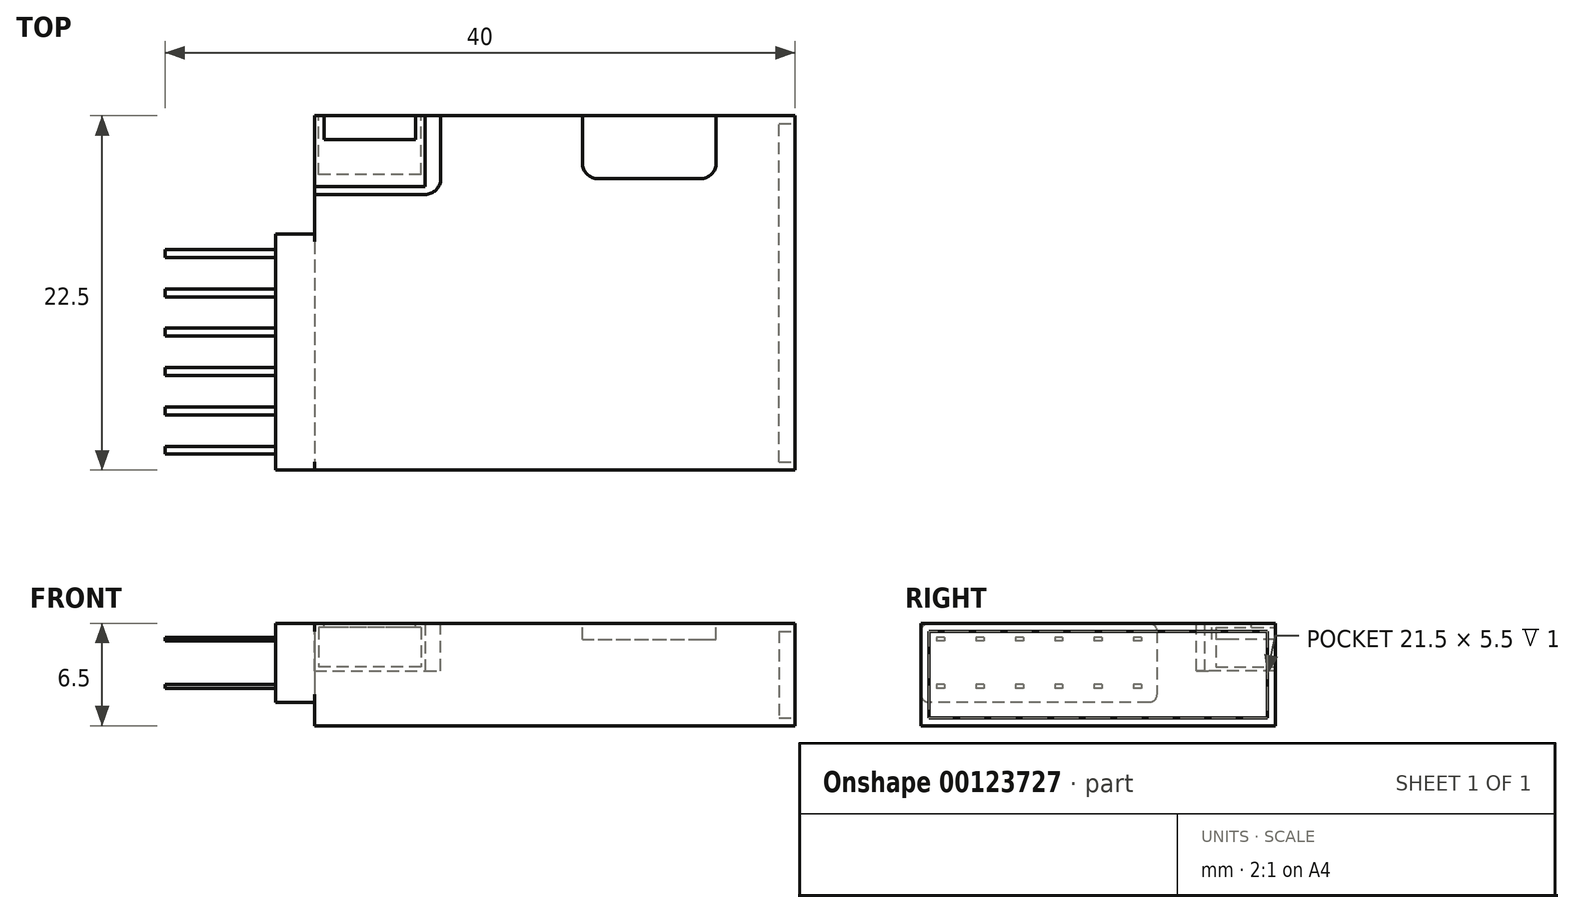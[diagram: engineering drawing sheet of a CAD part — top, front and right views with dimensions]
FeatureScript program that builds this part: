
annotation { "Feature Type Name" : "Feature", "Feature Type Description" : "" }
export const myFeature = defineFeature(function(context is Context, id is Id, definition is map)
    precondition{}
    {
        {
            var Q0;
            Q0=qCreatedBy(makeId("Top.planeOp"),FACE);
            var sketch = newSketch(context, id + "F0", { "sketchPlane" : qUnion([Q0])});
            skLineSegment(sketch, "E0.bottom", {"start": v(-15.25, 11.25) * mm, "end": v(15.25, 11.25) * mm});
            skLineSegment(sketch, "E0.top", {"start": v(-15.25, -11.25) * mm, "end": v(15.25, -11.25) * mm});
            skLineSegment(sketch, "E0.left", {"start": v(-15.25, 11.25) * mm, "end": v(-15.25, -11.25) * mm});
            skLineSegment(sketch, "E0.right", {"start": v(15.25, 11.25) * mm, "end": v(15.25, -11.25) * mm});
            skSolve(sketch);
        }
        {
            var Q0;
            Q0=qSketchRegion(id+"F0",true);
            extrude(context, id + "F1", {"entities" : qUnion([Q0]), "depth" : 6.5 * mm});
        }
        {
            var Q0;
            Q0=makeQuery(id+"F1.opExtrude","CAP_FACE",FACE,{"disambiguationData":[OSD([sQuery(id+"F0.wireOp",EDGE,"E0.bottom"),sQuery(id+"F0.wireOp",EDGE,"E0.top"),sQuery(id+"F0.wireOp",EDGE,"E0.left"),sQuery(id+"F0.wireOp",EDGE,"E0.right")])],"isStart":false});
            var sketch = newSketch(context, id + "F2", { "sketchPlane" : qUnion([Q0])});
            skLineSegment(sketch, "E1.bottom", {"start": v(-15.25, 11.25) * mm, "end": v(-7.25, 11.25) * mm});
            skLineSegment(sketch, "E1.top", {"start": v(-15.25, 6.25) * mm, "end": v(-8.25, 6.25) * mm});
            skLineSegment(sketch, "E1.left", {"start": v(-15.25, 11.25) * mm, "end": v(-15.25, 6.25) * mm});
            skLineSegment(sketch, "E1.right", {"start": v(-7.25, 11.25) * mm, "end": v(-7.25, 7.25) * mm});
            skPoint(sketch, "E2.visualSharp", {"position": v(-7.25, 6.25) * mm});
            skArc(sketch, "E2.filletArc", {"start": v(-8.25, 6.25) * mm, "mid": v(-7.54, 6.54) * mm, "end": v(-7.25, 7.25) * mm});
            skSolve(sketch);
        }
        {
            var Q0;
            Q0=qSketchRegion(id+"F2",true);
            extrude(context, id + "F3", {"entities" : qUnion([Q0]), "operationType" : NewBodyOperationType.REMOVE, "oppositeDirection" : true, "depth" : 3 * mm});
        }
        {
            var Q0;
            Q0=makeQuery(id+"F3.boolean.opBoolean","COPY",FACE,{"derivedFrom":makeQuery(id+"F3.opExtrude","CAP_FACE",FACE,{"disambiguationData":[OSD([sQuery(id+"F2.wireOp",EDGE,"E1.bottom"),sQuery(id+"F2.wireOp",EDGE,"E1.top"),sQuery(id+"F2.wireOp",EDGE,"E1.left"),sQuery(id+"F2.wireOp",EDGE,"E1.right"),sQuery(id+"F2.wireOp",EDGE,"E2.filletArc")])],"isStart":false})});
            var sketch = newSketch(context, id + "F4", { "sketchPlane" : qUnion([Q0])});
            skLineSegment(sketch, "E3.bottom", {"start": v(-15.25, 11.25) * mm, "end": v(-8.25, 11.25) * mm});
            skLineSegment(sketch, "E3.top", {"start": v(-15.25, 6.75) * mm, "end": v(-8.25, 6.75) * mm});
            skLineSegment(sketch, "E3.left", {"start": v(-15.25, 11.25) * mm, "end": v(-15.25, 6.75) * mm});
            skLineSegment(sketch, "E3.right", {"start": v(-8.25, 11.25) * mm, "end": v(-8.25, 6.75) * mm});
            skSolve(sketch);
        }
        {
            var Q0;
            Q0=qSketchRegion(id+"F4",true);
            extrude(context, id + "F5", {"entities" : qUnion([Q0]), "operationType" : NewBodyOperationType.ADD, "depth" : 3 * mm});
        }
        {
            var Q0;
            Q0=makeQuery(id+"F5.boolean.opBoolean","MERGE",FACE,{"derivedFrom":[makeQuery(id+"F1.opExtrude","SWEPT_FACE",FACE,{"disambiguationData":[OSD([sQuery(id+"F0.wireOp",EDGE,"E0.bottom")])]}),makeQuery(id+"F5.opExtrude","SWEPT_FACE",FACE,{"disambiguationData":[OSD([sQuery(id+"F4.wireOp",EDGE,"E3.bottom")])]})]});
            var sketch = newSketch(context, id + "F6", { "sketchPlane" : qUnion([Q0])});
            skLineSegment(sketch, "E4.bottom", {"start": v(8.5, 6.25) * mm, "end": v(15, 6.25) * mm});
            skLineSegment(sketch, "E4.top", {"start": v(8.5, 3.75) * mm, "end": v(15, 3.75) * mm});
            skLineSegment(sketch, "E4.left", {"start": v(8.5, 6.25) * mm, "end": v(8.5, 3.75) * mm});
            skLineSegment(sketch, "E4.right", {"start": v(15, 6.25) * mm, "end": v(15, 3.75) * mm});
            skSolve(sketch);
        }
        {
            var Q0;
            Q0=qSketchRegion(id+"F6",true);
            extrude(context, id + "F7", {"entities" : qUnion([Q0]), "operationType" : NewBodyOperationType.REMOVE, "oppositeDirection" : true, "depth" : 3.75 * mm});
        }
        {
            var Q0;
            Q0=makeQuery(id+"F5.opExtrude","CAP_FACE",FACE,{"disambiguationData":[OSD([sQuery(id+"F4.wireOp",EDGE,"E3.bottom"),sQuery(id+"F4.wireOp",EDGE,"E3.top"),sQuery(id+"F4.wireOp",EDGE,"E3.left"),sQuery(id+"F4.wireOp",EDGE,"E3.right")])],"isStart":false});
            var sketch = newSketch(context, id + "F8", { "sketchPlane" : qUnion([Q0])});
            skLineSegment(sketch, "E5.bottom", {"start": v(-14.65, 11.25) * mm, "end": v(-8.85, 11.25) * mm});
            skLineSegment(sketch, "E5.top", {"start": v(-14.65, 9.75) * mm, "end": v(-8.85, 9.75) * mm});
            skLineSegment(sketch, "E5.left", {"start": v(-14.65, 11.25) * mm, "end": v(-14.65, 9.75) * mm});
            skLineSegment(sketch, "E5.right", {"start": v(-8.85, 11.25) * mm, "end": v(-8.85, 9.75) * mm});
            skSolve(sketch);
        }
        {
            var Q0;
            Q0=qSketchRegion(id+"F8",true);
            extrude(context, id + "F9", {"entities" : qUnion([Q0]), "operationType" : NewBodyOperationType.REMOVE, "oppositeDirection" : true, "depth" : 0.5 * mm});
        }
        {
            var Q0;
            Q0=makeQuery(id+"F1.opExtrude","CAP_FACE",FACE,{"disambiguationData":[OSD([sQuery(id+"F0.wireOp",EDGE,"E0.bottom"),sQuery(id+"F0.wireOp",EDGE,"E0.top"),sQuery(id+"F0.wireOp",EDGE,"E0.left"),sQuery(id+"F0.wireOp",EDGE,"E0.right")])],"isStart":false});
            var sketch = newSketch(context, id + "F10", { "sketchPlane" : qUnion([Q0])});
            skLineSegment(sketch, "E6.bottom", {"start": v(1.75, 11.25) * mm, "end": v(10.25, 11.25) * mm});
            skLineSegment(sketch, "E6.top", {"start": v(2.75, 7.25) * mm, "end": v(9.25, 7.25) * mm});
            skLineSegment(sketch, "E6.left", {"start": v(1.75, 11.25) * mm, "end": v(1.75, 8.25) * mm});
            skLineSegment(sketch, "E6.right", {"start": v(10.25, 11.25) * mm, "end": v(10.25, 8.25) * mm});
            skPoint(sketch, "E7.visualSharp", {"position": v(1.75, 7.25) * mm});
            skArc(sketch, "E7.filletArc", {"start": v(1.75, 8.25) * mm, "mid": v(2.04, 7.54) * mm, "end": v(2.75, 7.25) * mm});
            skPoint(sketch, "E8.visualSharp", {"position": v(10.25, 7.25) * mm});
            skArc(sketch, "E8.filletArc", {"start": v(9.25, 7.25) * mm, "mid": v(9.96, 7.54) * mm, "end": v(10.25, 8.25) * mm});
            skSolve(sketch);
        }
        {
            var Q0;
            Q0=makeQuery(id+"F10.imprint","IMPRINT",FACE,{"disambiguationData":[TD([[makeQuery(id+"F10.imprint","IMPRINT",EDGE,{"derivedFrom":sQuery(id+"F10.wireOp",EDGE,"E6.bottom")}),-1.0]])]});
            extrude(context, id + "F11", {"entities" : qUnion([Q0]), "operationType" : NewBodyOperationType.REMOVE, "oppositeDirection" : true, "depth" : 1 * mm});
        }
        {
            var Q0;
            Q0=makeQuery(id+"F5.boolean.opBoolean","MERGE",FACE,{"derivedFrom":[makeQuery(id+"F1.opExtrude","SWEPT_FACE",FACE,{"disambiguationData":[OSD([sQuery(id+"F0.wireOp",EDGE,"E0.left")])]}),makeQuery(id+"F5.opExtrude","SWEPT_FACE",FACE,{"disambiguationData":[OSD([sQuery(id+"F4.wireOp",EDGE,"E3.left")])]})]});
            var sketch = newSketch(context, id + "F12", { "sketchPlane" : qUnion([Q0])});
            skLineSegment(sketch, "E9.bottom", {"start": v(-3.25, 6.5) * mm, "end": v(10.75, 6.5) * mm});
            skLineSegment(sketch, "E9.top", {"start": v(-3.25, 1.5) * mm, "end": v(10.75, 1.5) * mm});
            skLineSegment(sketch, "E9.left", {"start": v(-3.75, 6) * mm, "end": v(-3.75, 2) * mm});
            skLineSegment(sketch, "E9.right", {"start": v(11.25, 6) * mm, "end": v(11.25, 2) * mm});
            skPoint(sketch, "E10.visualSharp", {"position": v(-3.75, 6.5) * mm});
            skArc(sketch, "E10.filletArc", {"start": v(-3.25, 6.5) * mm, "mid": v(-3.6, 6.35) * mm, "end": v(-3.75, 6) * mm});
            skPoint(sketch, "E11.visualSharp", {"position": v(-3.75, 1.5) * mm});
            skArc(sketch, "E11.filletArc", {"start": v(-3.75, 2) * mm, "mid": v(-3.6, 1.65) * mm, "end": v(-3.25, 1.5) * mm});
            skPoint(sketch, "E12.visualSharp", {"position": v(11.25, 1.5) * mm});
            skArc(sketch, "E12.filletArc", {"start": v(10.75, 1.5) * mm, "mid": v(11.1, 1.65) * mm, "end": v(11.25, 2) * mm});
            skPoint(sketch, "E13.visualSharp", {"position": v(11.25, 6.5) * mm});
            skArc(sketch, "E13.filletArc", {"start": v(11.25, 6) * mm, "mid": v(11.1, 6.35) * mm, "end": v(10.75, 6.5) * mm});
            skSolve(sketch);
        }
        {
            var Q0;
            Q0=qSketchRegion(id+"F12",true);
            extrude(context, id + "F13", {"entities" : qUnion([Q0]), "operationType" : NewBodyOperationType.ADD, "depth" : 2.5 * mm});
        }
        {
            var Q0;
            Q0=makeQuery(id+"F13.opExtrude","CAP_FACE",FACE,{"disambiguationData":[OSD([sQuery(id+"F12.wireOp",EDGE,"E9.bottom"),sQuery(id+"F12.wireOp",EDGE,"E9.top"),sQuery(id+"F12.wireOp",EDGE,"E9.left"),sQuery(id+"F12.wireOp",EDGE,"E9.right"),sQuery(id+"F12.wireOp",EDGE,"E10.filletArc"),sQuery(id+"F12.wireOp",EDGE,"E11.filletArc"),sQuery(id+"F12.wireOp",EDGE,"E12.filletArc"),sQuery(id+"F12.wireOp",EDGE,"E13.filletArc")])],"isStart":false});
            var sketch = newSketch(context, id + "F14", { "sketchPlane" : qUnion([Q0])});
            skLineSegment(sketch, "E14.bottom", {"start": v(-2.75, 5.62) * mm, "end": v(-2.25, 5.62) * mm});
            skLineSegment(sketch, "E14.top", {"start": v(-2.75, 5.38) * mm, "end": v(-2.25, 5.38) * mm});
            skLineSegment(sketch, "E14.left", {"start": v(-2.75, 5.62) * mm, "end": v(-2.75, 5.38) * mm});
            skLineSegment(sketch, "E14.right", {"start": v(-2.25, 5.62) * mm, "end": v(-2.25, 5.38) * mm});
            skLineSegment(sketch, "E15.0.1.0", {"start": v(-2.75, 2.62) * mm, "end": v(-2.75, 2.37) * mm});
            skLineSegment(sketch, "E15.0.1.1", {"start": v(-2.25, 2.62) * mm, "end": v(-2.25, 2.37) * mm});
            skLineSegment(sketch, "E15.0.1.2", {"start": v(-2.75, 2.62) * mm, "end": v(-2.25, 2.62) * mm});
            skLineSegment(sketch, "E15.0.1.3", {"start": v(-2.75, 2.37) * mm, "end": v(-2.25, 2.37) * mm});
            skLineSegment(sketch, "E15.1.0.0", {"start": v(-0.25, 5.62) * mm, "end": v(-0.25, 5.38) * mm});
            skLineSegment(sketch, "E15.1.0.1", {"start": v(0.25, 5.62) * mm, "end": v(0.25, 5.38) * mm});
            skLineSegment(sketch, "E15.1.0.2", {"start": v(-0.25, 5.62) * mm, "end": v(0.25, 5.62) * mm});
            skLineSegment(sketch, "E15.1.0.3", {"start": v(-0.25, 5.38) * mm, "end": v(0.25, 5.38) * mm});
            skLineSegment(sketch, "E15.1.1.0", {"start": v(-0.25, 2.62) * mm, "end": v(-0.25, 2.37) * mm});
            skLineSegment(sketch, "E15.1.1.1", {"start": v(0.25, 2.62) * mm, "end": v(0.25, 2.37) * mm});
            skLineSegment(sketch, "E15.1.1.2", {"start": v(-0.25, 2.62) * mm, "end": v(0.25, 2.62) * mm});
            skLineSegment(sketch, "E15.1.1.3", {"start": v(-0.25, 2.37) * mm, "end": v(0.25, 2.37) * mm});
            skLineSegment(sketch, "E15.2.0.0", {"start": v(2.25, 5.62) * mm, "end": v(2.25, 5.38) * mm});
            skLineSegment(sketch, "E15.2.0.1", {"start": v(2.75, 5.62) * mm, "end": v(2.75, 5.38) * mm});
            skLineSegment(sketch, "E15.2.0.2", {"start": v(2.25, 5.62) * mm, "end": v(2.75, 5.62) * mm});
            skLineSegment(sketch, "E15.2.0.3", {"start": v(2.25, 5.38) * mm, "end": v(2.75, 5.38) * mm});
            skLineSegment(sketch, "E15.2.1.0", {"start": v(2.25, 2.62) * mm, "end": v(2.25, 2.37) * mm});
            skLineSegment(sketch, "E15.2.1.1", {"start": v(2.75, 2.62) * mm, "end": v(2.75, 2.37) * mm});
            skLineSegment(sketch, "E15.2.1.2", {"start": v(2.25, 2.62) * mm, "end": v(2.75, 2.62) * mm});
            skLineSegment(sketch, "E15.2.1.3", {"start": v(2.25, 2.37) * mm, "end": v(2.75, 2.37) * mm});
            skLineSegment(sketch, "E15.3.0.0", {"start": v(4.75, 5.62) * mm, "end": v(4.75, 5.38) * mm});
            skLineSegment(sketch, "E15.3.0.1", {"start": v(5.25, 5.62) * mm, "end": v(5.25, 5.38) * mm});
            skLineSegment(sketch, "E15.3.0.2", {"start": v(4.75, 5.62) * mm, "end": v(5.25, 5.62) * mm});
            skLineSegment(sketch, "E15.3.0.3", {"start": v(4.75, 5.38) * mm, "end": v(5.25, 5.38) * mm});
            skLineSegment(sketch, "E15.3.1.0", {"start": v(4.75, 2.62) * mm, "end": v(4.75, 2.37) * mm});
            skLineSegment(sketch, "E15.3.1.1", {"start": v(5.25, 2.62) * mm, "end": v(5.25, 2.37) * mm});
            skLineSegment(sketch, "E15.3.1.2", {"start": v(4.75, 2.62) * mm, "end": v(5.25, 2.62) * mm});
            skLineSegment(sketch, "E15.3.1.3", {"start": v(4.75, 2.37) * mm, "end": v(5.25, 2.37) * mm});
            skLineSegment(sketch, "E15.4.0.0", {"start": v(7.25, 5.62) * mm, "end": v(7.25, 5.38) * mm});
            skLineSegment(sketch, "E15.4.0.1", {"start": v(7.75, 5.62) * mm, "end": v(7.75, 5.38) * mm});
            skLineSegment(sketch, "E15.4.0.2", {"start": v(7.25, 5.62) * mm, "end": v(7.75, 5.62) * mm});
            skLineSegment(sketch, "E15.4.0.3", {"start": v(7.25, 5.38) * mm, "end": v(7.75, 5.38) * mm});
            skLineSegment(sketch, "E15.4.1.0", {"start": v(7.25, 2.62) * mm, "end": v(7.25, 2.37) * mm});
            skLineSegment(sketch, "E15.4.1.1", {"start": v(7.75, 2.62) * mm, "end": v(7.75, 2.37) * mm});
            skLineSegment(sketch, "E15.4.1.2", {"start": v(7.25, 2.62) * mm, "end": v(7.75, 2.62) * mm});
            skLineSegment(sketch, "E15.4.1.3", {"start": v(7.25, 2.37) * mm, "end": v(7.75, 2.37) * mm});
            skLineSegment(sketch, "E15.5.0.0", {"start": v(9.75, 5.62) * mm, "end": v(9.75, 5.38) * mm});
            skLineSegment(sketch, "E15.5.0.1", {"start": v(10.25, 5.62) * mm, "end": v(10.25, 5.38) * mm});
            skLineSegment(sketch, "E15.5.0.2", {"start": v(9.75, 5.62) * mm, "end": v(10.25, 5.62) * mm});
            skLineSegment(sketch, "E15.5.0.3", {"start": v(9.75, 5.38) * mm, "end": v(10.25, 5.38) * mm});
            skLineSegment(sketch, "E15.5.1.0", {"start": v(9.75, 2.62) * mm, "end": v(9.75, 2.37) * mm});
            skLineSegment(sketch, "E15.5.1.1", {"start": v(10.25, 2.62) * mm, "end": v(10.25, 2.37) * mm});
            skLineSegment(sketch, "E15.5.1.2", {"start": v(9.75, 2.62) * mm, "end": v(10.25, 2.62) * mm});
            skLineSegment(sketch, "E15.5.1.3", {"start": v(9.75, 2.37) * mm, "end": v(10.25, 2.37) * mm});
            skLineSegment(sketch, "E15.direction1", {"start": v(-2.75, 5.38) * mm, "end": v(-0.25, 5.38) * mm, "construction": true});
            skLineSegment(sketch, "E15.direction2", {"start": v(-2.75, 5.38) * mm, "end": v(-2.75, 2.37) * mm, "construction": true});
            skLineSegment(sketch, "E16", {"start": v(3.75, 6.5) * mm, "end": v(3.75, 1.5) * mm, "construction": true});
            skLineSegment(sketch, "E17", {"start": v(-3.75, 4) * mm, "end": v(11.25, 4) * mm, "construction": true});
            skSolve(sketch);
        }
        {
            var Q0;
            Q0=qSketchRegion(id+"F14",true);
            extrude(context, id + "F15", {"entities" : qUnion([Q0]), "operationType" : NewBodyOperationType.ADD, "depth" : 7 * mm});
        }
        {
            var Q0;
            Q0=makeQuery(id+"F1.opExtrude","SWEPT_FACE",FACE,{"disambiguationData":[OSD([sQuery(id+"F0.wireOp",EDGE,"E0.right")])]});
            var sketch = newSketch(context, id + "F16", { "sketchPlane" : qUnion([Q0])});
            skLineSegment(sketch, "E18.bottom", {"start": v(-10.75, 6) * mm, "end": v(10.75, 6) * mm});
            skLineSegment(sketch, "E18.top", {"start": v(-10.75, 0.5) * mm, "end": v(10.75, 0.5) * mm});
            skLineSegment(sketch, "E18.left", {"start": v(-10.75, 6) * mm, "end": v(-10.75, 0.5) * mm});
            skLineSegment(sketch, "E18.right", {"start": v(10.75, 6) * mm, "end": v(10.75, 0.5) * mm});
            skSolve(sketch);
        }
        {
            var Q0;
            Q0=qSketchRegion(id+"F16",true);
            extrude(context, id + "F17", {"entities" : qUnion([Q0]), "operationType" : NewBodyOperationType.REMOVE, "oppositeDirection" : true, "depth" : 1 * mm});
        }
    });
